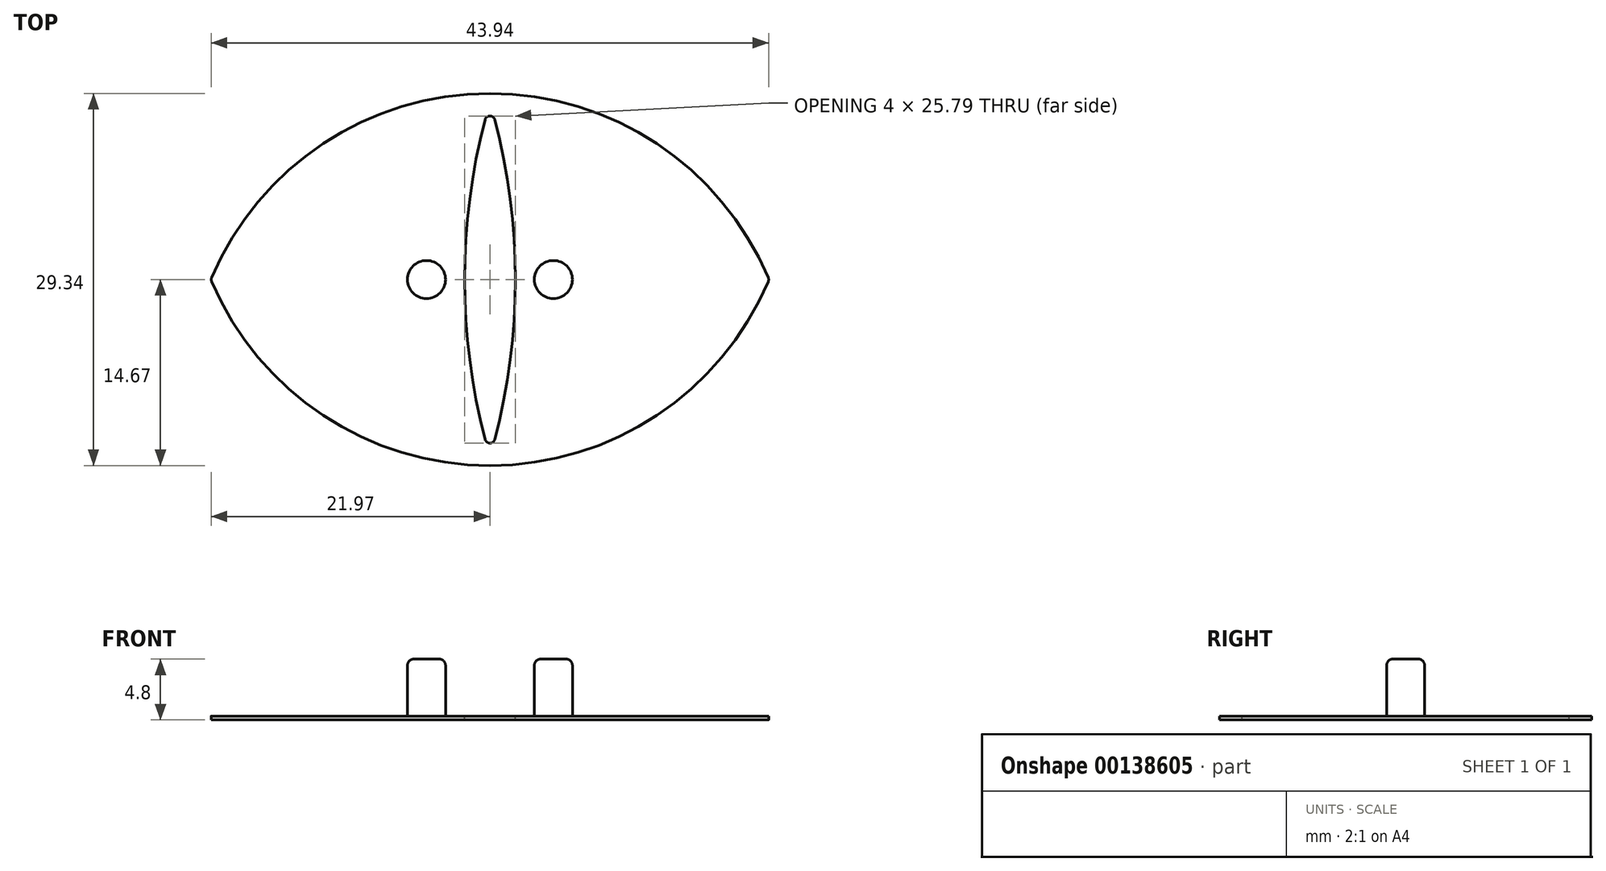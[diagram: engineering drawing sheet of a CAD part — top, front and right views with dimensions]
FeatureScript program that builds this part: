
annotation { "Feature Type Name" : "Feature", "Feature Type Description" : "" }
export const myFeature = defineFeature(function(context is Context, id is Id, definition is map)
    precondition{}
    {
        {
            assignVariable(context, id + "F0", {"name" : "pin_end_fillet", "anyValue" : 0.5 * mm});
        }
        {
            assignVariable(context, id + "F1", {"name" : "pin_length", "anyValue" : 4.5 * mm});
        }
        {
            var Q0;
            Q0=qCreatedBy(makeId("Top.planeOp"),FACE);
            var sketch = newSketch(context, id + "F2", { "sketchPlane" : qUnion([Q0])});
            skCircle(sketch, "E0", {"center": v(0, 0) * mm, "radius": 22 * mm, "construction": true});
            skLineSegment(sketch, "E1", {"start": v(-22, 0) * mm, "end": v(22, 0) * mm, "construction": true});
            skLineSegment(sketch, "E2", {"start": v(0, 22) * mm, "end": v(0, 14.67) * mm, "construction": true});
            skLineSegment(sketch, "E3", {"start": v(0, 14.67) * mm, "end": v(0, 7.33) * mm, "construction": true});
            skLineSegment(sketch, "E4", {"start": v(0, 7.33) * mm, "end": v(0, 0) * mm, "construction": true});
            skArc(sketch, "E5", {"start": v(21.93, 0.16) * mm, "mid": v(0, 14.67) * mm, "end": v(-21.93, 0.16) * mm});
            skArc(sketch, "E6.MirrorCS", {"start": v(21.93, -0.16) * mm, "mid": v(0, -14.67) * mm, "end": v(-21.93, -0.16) * mm});
            skPoint(sketch, "E7.visualSharp", {"position": v(22, 0) * mm});
            skArc(sketch, "E7.filletArc", {"start": v(21.93, -0.16) * mm, "mid": v(21.97, 0) * mm, "end": v(21.93, 0.16) * mm});
            skPoint(sketch, "E8.visualSharp", {"position": v(-22, 0) * mm});
            skArc(sketch, "E8.filletArc", {"start": v(-21.93, 0.16) * mm, "mid": v(-21.97, 0) * mm, "end": v(-21.93, -0.16) * mm});
            skSolve(sketch);
        }
        {
            var Q0;
            Q0=makeQuery(id+"F2.imprint","IMPRINT",FACE,{"disambiguationData":[TD([[makeQuery(id+"F2.imprint","IMPRINT",EDGE,{"derivedFrom":sQuery(id+"F2.wireOp",EDGE,"E5")}),1.0]])]});
            extrude(context, id + "F3", {"entities" : qUnion([Q0]), "depth" : 0.3 * mm});
        }
        {
            var Q0;
            Q0=makeQuery(id+"F3.opExtrude","CAP_FACE",FACE,{"disambiguationData":[OSD([sQuery(id+"F2.wireOp",EDGE,"E5"),sQuery(id+"F2.wireOp",EDGE,"E6.MirrorCS"),sQuery(id+"F2.wireOp",EDGE,"E7.filletArc"),sQuery(id+"F2.wireOp",EDGE,"E8.filletArc")])],"isStart":false});
            var sketch = newSketch(context, id + "F4", { "sketchPlane" : qUnion([Q0])});
            skLineSegment(sketch, "E9", {"start": v(0, 0) * mm, "end": v(5, 0) * mm, "construction": true});
            skLineSegment(sketch, "E10", {"start": v(0, 0) * mm, "end": v(-5, 0) * mm, "construction": true});
            skCircle(sketch, "E11", {"center": v(5, 0) * mm, "radius": 1.5 * mm});
            skCircle(sketch, "E12", {"center": v(-5, 0) * mm, "radius": 1.5 * mm});
            skSolve(sketch);
        }
        {
            var Q0;
            Q0=makeQuery(id+"F4.imprint","IMPRINT",FACE,{"disambiguationData":[TD([[makeQuery(id+"F4.imprint","IMPRINT",EDGE,{"derivedFrom":sQuery(id+"F4.wireOp",EDGE,"E12")}),1.0]])]});
            var Q1;
            Q1=makeQuery(id+"F4.imprint","IMPRINT",FACE,{"disambiguationData":[TD([[makeQuery(id+"F4.imprint","IMPRINT",EDGE,{"derivedFrom":sQuery(id+"F4.wireOp",EDGE,"E11")}),1.0]])]});
            extrude(context, id + "F5", {"entities" : qUnion([Q0, Q1]), "operationType" : NewBodyOperationType.ADD, "depth" : getVariable(context, 'pin_length')});
        }
        {
            var Q0;
            Q0=makeQuery(id+"F5.opExtrude","CAP_EDGE",EDGE,{"disambiguationData":[OSD([sQuery(id+"F4.wireOp",EDGE,"E12")])],"isStart":false});
            var Q1;
            Q1=makeQuery(id+"F5.opExtrude","CAP_EDGE",EDGE,{"disambiguationData":[OSD([sQuery(id+"F4.wireOp",EDGE,"E11")])],"isStart":false});
            fillet(context, id + "F6", {"entities" : qUnion([Q0, Q1]), "radius" : getVariable(context, 'pin_end_fillet'), "tangentPropagation" : true, "allowEdgeOverflow" : false});
        }
        {
            var Q0;
            Q0=makeQuery(id+"F3.opExtrude","CAP_FACE",FACE,{"disambiguationData":[OSD([sQuery(id+"F2.wireOp",EDGE,"E5"),sQuery(id+"F2.wireOp",EDGE,"E6.MirrorCS"),sQuery(id+"F2.wireOp",EDGE,"E7.filletArc"),sQuery(id+"F2.wireOp",EDGE,"E8.filletArc")])],"isStart":false});
            var sketch = newSketch(context, id + "F7", { "sketchPlane" : qUnion([Q0])});
            skLineSegment(sketch, "E13", {"start": v(0, 0) * mm, "end": v(0, 14) * mm, "construction": true});
            skLineSegment(sketch, "E14", {"start": v(0, 0) * mm, "end": v(2, 0) * mm, "construction": true});
            skLineSegment(sketch, "E15.MirrorCS", {"start": v(0, 0) * mm, "end": v(0, -14) * mm, "construction": true});
            skArc(sketch, "E16", {"start": v(0.39, -12.6) * mm, "mid": v(2, 0) * mm, "end": v(0.39, 12.6) * mm});
            skArc(sketch, "E17.MirrorCS", {"start": v(-0.39, -12.6) * mm, "mid": v(-2, 0) * mm, "end": v(-0.39, 12.6) * mm});
            skPoint(sketch, "E18.visualSharp", {"position": v(0, 14) * mm});
            skArc(sketch, "E18.filletArc", {"start": v(0.39, 12.6) * mm, "mid": v(0, 12.9) * mm, "end": v(-0.39, 12.6) * mm});
            skPoint(sketch, "E19.visualSharp", {"position": v(0, -14) * mm});
            skArc(sketch, "E19.filletArc", {"start": v(-0.39, -12.6) * mm, "mid": v(0, -12.9) * mm, "end": v(0.39, -12.6) * mm});
            skSolve(sketch);
        }
        {
            var Q0;
            Q0=makeQuery(id+"F7.imprint","IMPRINT",FACE,{"disambiguationData":[TD([[makeQuery(id+"F7.imprint","IMPRINT",EDGE,{"derivedFrom":sQuery(id+"F7.wireOp",EDGE,"E16")}),1.0]])]});
            extrude(context, id + "F8", {"entities" : qUnion([Q0]), "operationType" : NewBodyOperationType.REMOVE, "endBound" : BoundingType.THROUGH_ALL, "oppositeDirection" : true, "depth" : 25.4 * mm});
        }
    });
